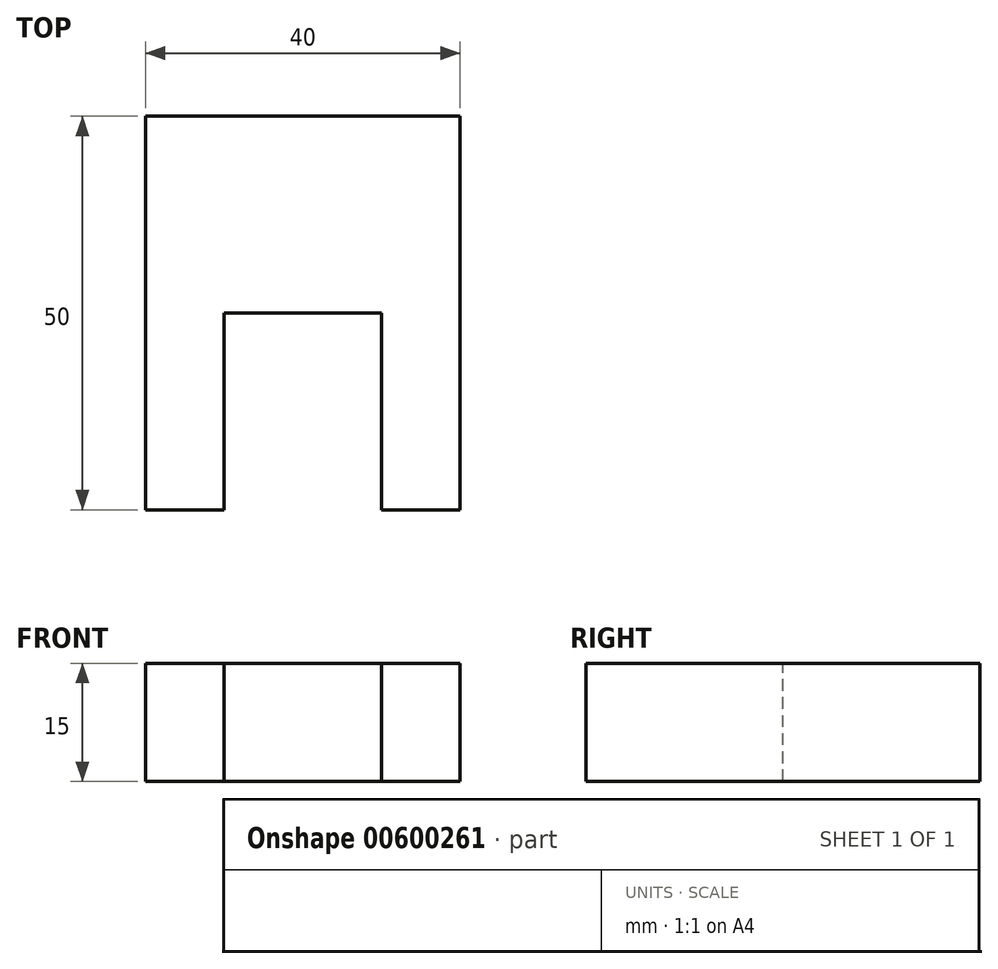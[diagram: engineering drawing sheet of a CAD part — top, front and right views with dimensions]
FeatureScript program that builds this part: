
annotation { "Feature Type Name" : "Feature", "Feature Type Description" : "" }
export const myFeature = defineFeature(function(context is Context, id is Id, definition is map)
    precondition{}
    {
        {
            var Q0;
            Q0=qCreatedBy(makeId("Right.planeOp"),FACE);
            var sketch = newSketch(context, id + "F0", { "sketchPlane" : qUnion([Q0])});
            skLineSegment(sketch, "E0.bottom", {"start": v(0, 0) * mm, "end": v(50, 0) * mm});
            skLineSegment(sketch, "E0.top", {"start": v(0, 15) * mm, "end": v(50, 15) * mm});
            skLineSegment(sketch, "E0.left", {"start": v(0, 0) * mm, "end": v(0, 15) * mm});
            skLineSegment(sketch, "E0.right", {"start": v(50, 0) * mm, "end": v(50, 15) * mm});
            skSolve(sketch);
        }
        {
            var Q0;
            Q0 = qSketchRegion(id + "F0", true);
            extrude(context, id + "F1", {"entities" : qUnion([Q0]), "depth" : 40 * mm, "offsetDistance" : 25 * mm});
        }
        {
            var Q0;
            Q0=makeQuery(id+"F1.opExtrude","SWEPT_FACE",FACE,{"disambiguationData":[OSD([sQuery(id+"F0.wireOp",EDGE,"E0.top")])]});
            var sketch = newSketch(context, id + "F2", { "sketchPlane" : qUnion([Q0])});
            skLineSegment(sketch, "E1.bottom", {"start": v(10, 0) * mm, "end": v(30, 0) * mm});
            skLineSegment(sketch, "E1.top", {"start": v(10, 25) * mm, "end": v(30, 25) * mm});
            skLineSegment(sketch, "E1.left", {"start": v(10, 0) * mm, "end": v(10, 25) * mm});
            skLineSegment(sketch, "E1.right", {"start": v(30, 0) * mm, "end": v(30, 25) * mm});
            skSolve(sketch);
        }
        {
            var Q0;
            Q0=makeQuery(id+"F2.imprint","IMPRINT",FACE,{"disambiguationData":[TD([[makeQuery(id+"F2.imprint","IMPRINT",EDGE,{"derivedFrom":sQuery(id+"F2.wireOp",EDGE,"E1.bottom")}),-1.0]])]});
            extrude(context, id + "F3", {"entities" : qUnion([Q0]), "operationType" : NewBodyOperationType.REMOVE, "oppositeDirection" : true, "depth" : 25 * mm, "offsetDistance" : 25 * mm});
        }
    });
